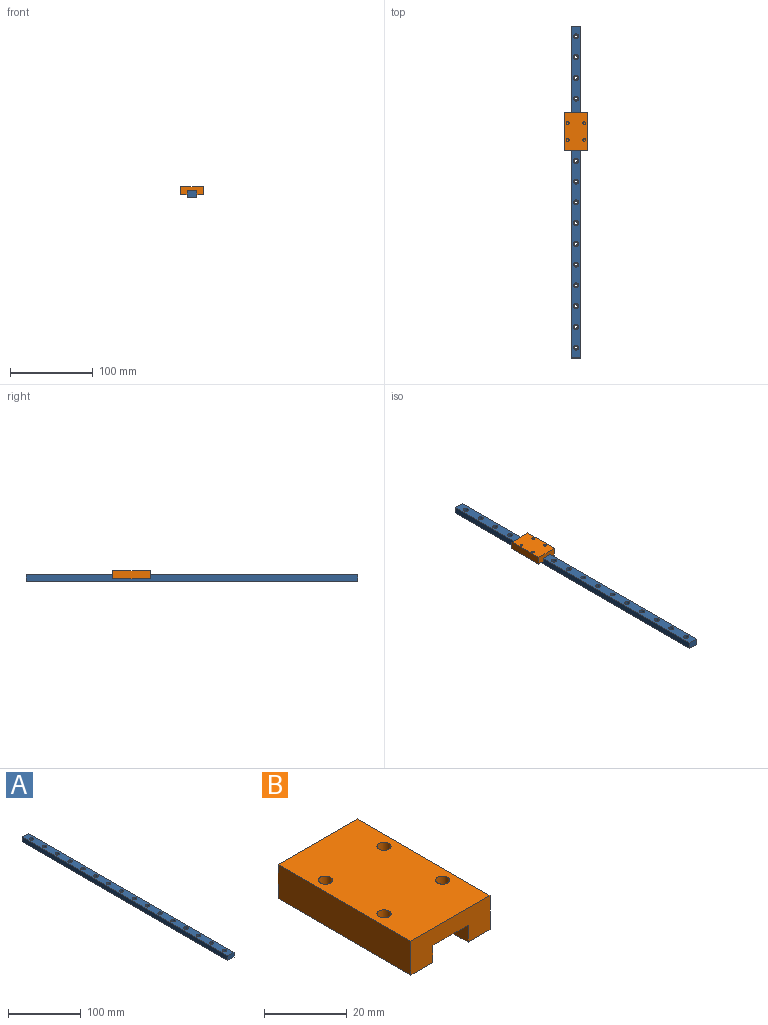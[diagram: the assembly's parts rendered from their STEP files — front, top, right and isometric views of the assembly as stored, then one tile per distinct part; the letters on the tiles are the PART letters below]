
ASSEMBLY  parts=2 mates=1
PART A: 54 faces, bbox 12x400x8 mm
  f0: plane 400x8mm, normal (1,0,0), area 3200mm2, adj f1,f3,f4,f5
  f1: plane 12x8mm, normal (0,1,0), area 96mm2, adj f0,f2,f4,f5
  f2: plane 400x8mm, normal (-1,0,0), area 3200mm2, adj f1,f3,f4,f5
  f3: plane 12x8mm, normal (0,-1,0), area 96mm2, adj f0,f2,f4,f5
  f4: plane 400x12mm, normal (0,0,-1), area 4646.1mm2, adj f0,f1,f2,f3,f6,f9,f12,f15
  f5: plane 400x12mm, normal (0,0,1), area 4347.6mm2, adj f0,f1,f2,f3,f8,f11,f14,f17
  f6: cylinder r=1.75mm len=3.5mm, axis (0,0,1), area 38.5mm2, adj f4,f7
  f7: plane 6x6mm, normal (0,0,1), area 18.7mm2, adj f6,f8
  f8: cylinder r=3mm len=6mm, axis (0,0,1), area 84.8mm2, adj f5,f7
  f9: cylinder r=1.75mm len=3.5mm, axis (0,0,1), area 38.5mm2, adj f4,f10
  f10: plane 6x6mm, normal (0,0,1), area 18.7mm2, adj f9,f11
  f11: cylinder r=3mm len=6mm, axis (0,0,1), area 84.8mm2, adj f5,f10
  f12: cylinder r=1.75mm len=3.5mm, axis (0,0,1), area 38.5mm2, adj f4,f13
  f13: plane 6x6mm, normal (0,0,1), area 18.7mm2, adj f12,f14
  f14: cylinder r=3mm len=6mm, axis (0,0,1), area 84.8mm2, adj f5,f13
  f15: cylinder r=1.75mm len=3.5mm, axis (0,0,1), area 38.5mm2, adj f4,f16
  f16: plane 6x6mm, normal (0,0,1), area 18.7mm2, adj f15,f17
  f17: cylinder r=3mm len=6mm, axis (0,0,1), area 84.8mm2, adj f5,f16
  f18: cylinder r=1.75mm len=3.5mm, axis (0,0,1), area 38.5mm2, adj f4,f19
  f19: plane 6x6mm, normal (0,0,1), area 18.7mm2, adj f18,f20
  f20: cylinder r=3mm len=6mm, axis (0,0,1), area 84.8mm2, adj f5,f19
  f21: cylinder r=1.75mm len=3.5mm, axis (0,0,1), area 38.5mm2, adj f4,f22
  f22: plane 6x6mm, normal (0,0,1), area 18.7mm2, adj f21,f23
  f23: cylinder r=3mm len=6mm, axis (0,0,1), area 84.8mm2, adj f5,f22
  f24: cylinder r=1.75mm len=3.5mm, axis (0,0,1), area 38.5mm2, adj f4,f25
  f25: plane 6x6mm, normal (0,0,1), area 18.7mm2, adj f24,f26
  f26: cylinder r=3mm len=6mm, axis (0,0,1), area 84.8mm2, adj f5,f25
  f27: cylinder r=1.75mm len=3.5mm, axis (0,0,1), area 38.5mm2, adj f4,f28
  f28: plane 6x6mm, normal (0,0,1), area 18.7mm2, adj f27,f29
  f29: cylinder r=3mm len=6mm, axis (0,0,1), area 84.8mm2, adj f5,f28
  f30: cylinder r=1.75mm len=3.5mm, axis (0,0,1), area 38.5mm2, adj f4,f31
  f31: plane 6x6mm, normal (0,0,1), area 18.7mm2, adj f30,f32
  f32: cylinder r=3mm len=6mm, axis (0,0,1), area 84.8mm2, adj f5,f31
  f33: cylinder r=1.75mm len=3.5mm, axis (0,0,1), area 38.5mm2, adj f4,f34
  f34: plane 6x6mm, normal (0,0,1), area 18.7mm2, adj f33,f35
  f35: cylinder r=3mm len=6mm, axis (0,0,1), area 84.8mm2, adj f5,f34
  f36: cylinder r=1.75mm len=3.5mm, axis (0,0,1), area 38.5mm2, adj f4,f37
  f37: plane 6x6mm, normal (0,0,1), area 18.7mm2, adj f36,f38
  f38: cylinder r=3mm len=6mm, axis (0,0,1), area 84.8mm2, adj f5,f37
  f39: cylinder r=1.75mm len=3.5mm, axis (0,0,1), area 38.5mm2, adj f4,f40
  f40: plane 6x6mm, normal (0,0,1), area 18.7mm2, adj f39,f41
  f41: cylinder r=3mm len=6mm, axis (0,0,1), area 84.8mm2, adj f5,f40
  f42: cylinder r=1.75mm len=3.5mm, axis (0,0,1), area 38.5mm2, adj f4,f43
  f43: plane 6x6mm, normal (0,0,1), area 18.7mm2, adj f42,f44
  f44: cylinder r=3mm len=6mm, axis (0,0,1), area 84.8mm2, adj f5,f43
  f45: cylinder r=1.75mm len=3.5mm, axis (0,0,1), area 38.5mm2, adj f4,f46
  f46: plane 6x6mm, normal (0,0,1), area 18.7mm2, adj f45,f47
  f47: cylinder r=3mm len=6mm, axis (0,0,1), area 84.8mm2, adj f5,f46
  f48: cylinder r=1.75mm len=3.5mm, axis (0,0,1), area 38.5mm2, adj f4,f49
  f49: plane 6x6mm, normal (0,0,1), area 18.7mm2, adj f48,f50
  f50: cylinder r=3mm len=6mm, axis (0,0,1), area 84.8mm2, adj f5,f49
  f51: cylinder r=1.75mm len=3.5mm, axis (0,0,1), area 38.5mm2, adj f4,f52
  f52: plane 6x6mm, normal (0,0,1), area 18.7mm2, adj f51,f53
  f53: cylinder r=3mm len=6mm, axis (0,0,1), area 84.8mm2, adj f5,f52
PART B: 18 faces, bbox 27x45.4x10 mm
  f0: plane 45.4x7.5mm, normal (0,0,-1), area 340.5mm2, adj f1,f2,f3,f15
  f1: plane 27x10mm, normal (0,1,0), area 210mm2, adj f0,f3,f4,f5,f6,f15,f16,f17
  f2: plane 27x10mm, normal (0,-1,0), area 210mm2, adj f0,f3,f4,f5,f6,f15,f16,f17
  f3: plane 45.4x10mm, normal (1,0,0), area 454mm2, adj f0,f1,f2,f6
  f4: plane 45.4x10mm, normal (-1,0,0), area 454mm2, adj f1,f2,f5,f6
  f5: plane 45.4x7.5mm, normal (0,0,-1), area 340.5mm2, adj f1,f2,f4,f17
  f6: plane 45.4x27mm, normal (0,0,1), area 1189.5mm2, adj f1,f2,f3,f4,f8,f10,f12,f14
  f7: cone r=0mm half-angle=59deg, axis (0,0,1), area 10.6mm2, adj f8
  f8: cylinder r=1.7mm len=3.4mm, axis (0,0,1), area 32mm2, adj f6,f7
  f9: cone r=0mm half-angle=59deg, axis (0,0,1), area 10.6mm2, adj f10
  f10: cylinder r=1.7mm len=3.4mm, axis (0,0,1), area 32mm2, adj f6,f9
  f11: cone r=0mm half-angle=59deg, axis (0,0,1), area 10.6mm2, adj f12
  f12: cylinder r=1.7mm len=3.4mm, axis (0,0,1), area 32mm2, adj f6,f11
  f13: cone r=0mm half-angle=59deg, axis (0,0,1), area 10.6mm2, adj f14
  f14: cylinder r=1.7mm len=3.4mm, axis (0,0,1), area 32mm2, adj f6,f13
  f15: plane 45.4x5mm, normal (-1,0,0), area 227mm2, adj f0,f1,f2,f16
  f16: plane 45.4x12mm, normal (0,0,-1), area 544.8mm2, adj f1,f2,f15,f17
  f17: plane 45.4x5mm, normal (1,0,0), area 227mm2, adj f1,f2,f5,f16
PLACE A at identity fixed
PLACE B t=(0,72.88,5)mm
MATE slider B.f2 <-> A.f3  axis (0,-1,0) through (0,50.18,0)mm
